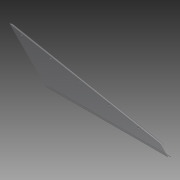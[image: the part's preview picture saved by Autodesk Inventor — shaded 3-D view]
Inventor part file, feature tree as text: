
AUTODESK INVENTOR PART (.ipt)
format: ipt  version: 2014 SP1 (Build 180222100, 222)  size: 88,064 bytes
history: native  units: in
note: dims shown in document units (in); Inventor stores cm internally (conversion verified against a paired STEP export)
features: reference x2, extrude x1, sketch x1
ambient origin geometry x8: Origin, YZ Plane, XZ Plane, XY Plane, X Axis, Y Axis, Z Axis, Center Point
bodies: Solid1 (feature_tree)
feature tree (4):
  extrude  "Extrusion1"  Depth=0.25in
  sketch  "Sketch1"  dims[d0=3.5in d1=18.75in d3=0.125in d4=0.0in d5=4.0in d6=0.25in]
  reference  "Reference1"
  reference  "Reference2"
